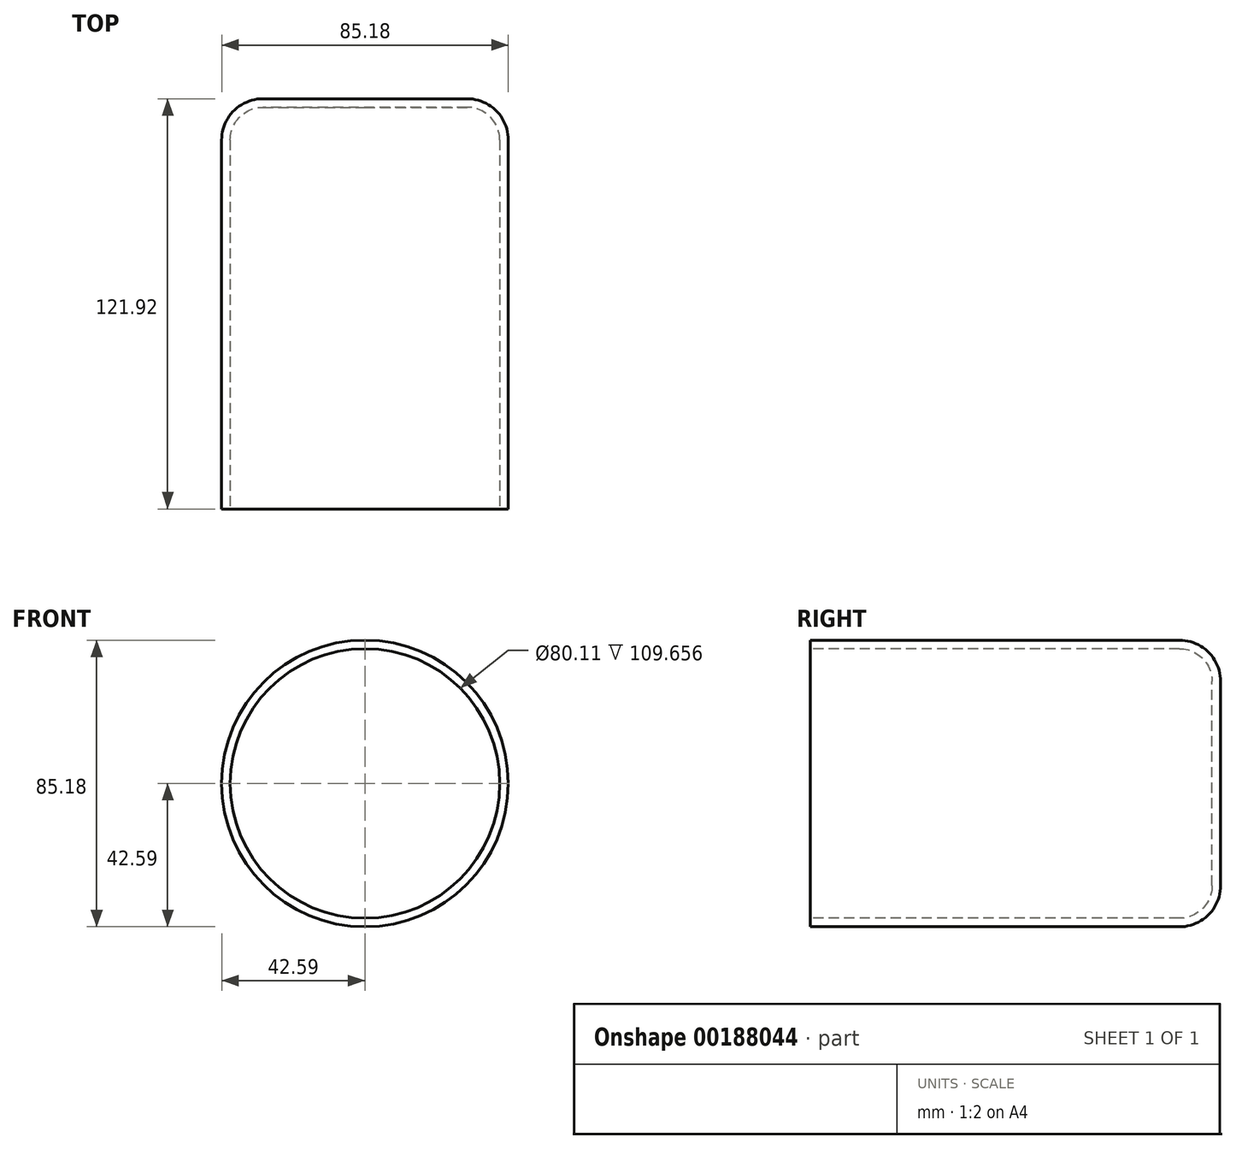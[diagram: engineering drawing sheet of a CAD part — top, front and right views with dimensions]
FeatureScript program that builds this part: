
annotation { "Feature Type Name" : "Feature", "Feature Type Description" : "" }
export const myFeature = defineFeature(function(context is Context, id is Id, definition is map)
    precondition{}
    {
        {
            var Q0;
            Q0=qCreatedBy(makeId("Front.planeOp"),FACE);
            var sketch = newSketch(context, id + "F0", { "sketchPlane" : qUnion([Q0])});
            skCircle(sketch, "E0", {"center": v(0, 0) * mm, "radius": 42.6 * mm});
            skSolve(sketch);
        }
        {
            var Q0;
            Q0 = qSketchRegion(id + "F0", true);
            extrude(context, id + "F1", {"entities" : qUnion([Q0]), "oppositeDirection" : true, "depth" : 121.92 * mm});
        }
        {
            var Q0;
            Q0=makeQuery(id+"F1.opExtrude","CAP_EDGE",EDGE,{"disambiguationData":[OSD([sQuery(id+"F0.wireOp",EDGE,"E0")])],"isStart":false});
            fillet(context, id + "F2", {"entities" : qUnion([Q0]), "radius" : 12.26 * mm, "tangentPropagation" : true, "allowEdgeOverflow" : false});
        }
        {
            var Q0;
            Q0=makeQuery(id+"F1.opExtrude","CAP_FACE",FACE,{"disambiguationData":[OSD([sQuery(id+"F0.wireOp",EDGE,"E0")])],"isStart":true});
            shell(context, id + "F3", {"entities" : qUnion([Q0]), "thickness" : 2.54 * mm});
        }
    });
